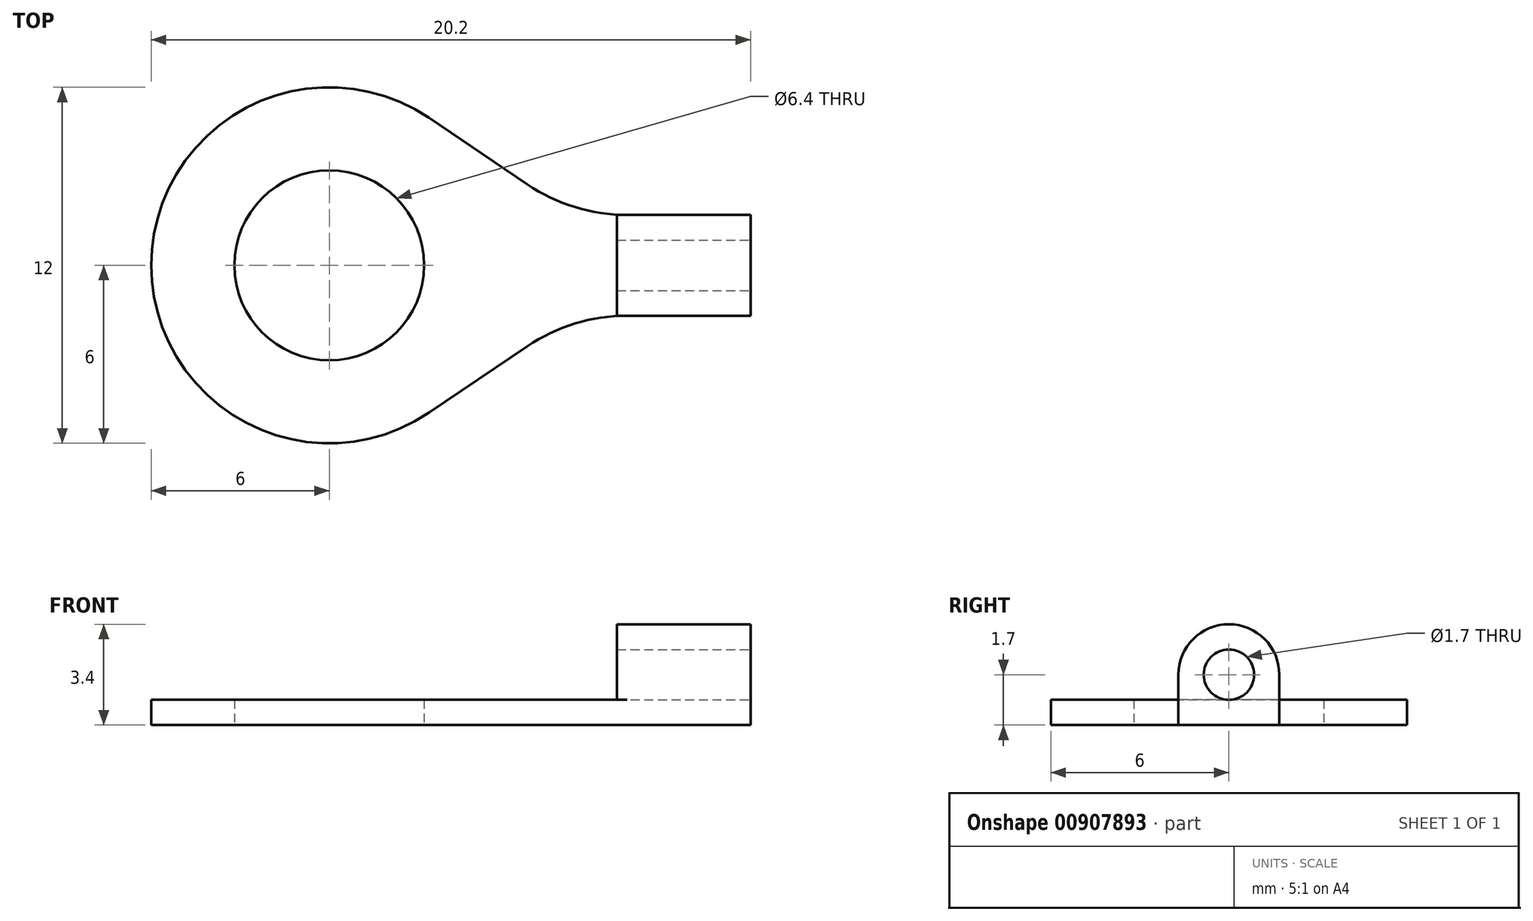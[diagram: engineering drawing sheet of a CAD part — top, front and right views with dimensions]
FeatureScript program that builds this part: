
annotation { "Feature Type Name" : "Feature", "Feature Type Description" : "" }
export const myFeature = defineFeature(function(context is Context, id is Id, definition is map)
    precondition{}
    {
        {
            var Q0;
            Q0=qCreatedBy(makeId("Top.planeOp"),FACE);
            var sketch = newSketch(context, id + "F0", { "sketchPlane" : qUnion([Q0])});
            skLineSegment(sketch, "E0.left", {"start": v(0, 6) * mm, "end": v(0, 6) * mm});
            skLineSegment(sketch, "E0.right", {"start": v(20.2, 4.3) * mm, "end": v(20.2, 7.7) * mm});
            skPoint(sketch, "E1.visualSharp", {"position": v(0, 12) * mm});
            skArc(sketch, "E1.filletArc", {"start": v(6, 12) * mm, "mid": v(1.76, 10.24) * mm, "end": v(0, 6) * mm});
            skPoint(sketch, "E2.visualSharp", {"position": v(0, 0) * mm});
            skArc(sketch, "E2.filletArc", {"start": v(0, 6) * mm, "mid": v(1.76, 1.76) * mm, "end": v(6, 0) * mm});
            skLineSegment(sketch, "E3.bottom", {"start": v(20.2, 4.3) * mm, "end": v(16.04, 4.3) * mm});
            skLineSegment(sketch, "E3.top", {"start": v(20.2, 7.7) * mm, "end": v(16.04, 7.7) * mm});
            skPoint(sketch, "E3.middle", {"position": v(20.2, 6) * mm});
            skArc(sketch, "E4", {"start": v(9.36, 10.97) * mm, "mid": v(0, 6) * mm, "end": v(9.36, 1.03) * mm});
            skCircle(sketch, "E5", {"center": v(6, 6) * mm, "radius": 3.2 * mm});
            skLineSegment(sketch, "E6", {"start": v(12.68, 8.73) * mm, "end": v(9.36, 10.97) * mm});
            skLineSegment(sketch, "E7", {"start": v(12.68, 3.27) * mm, "end": v(9.36, 1.03) * mm});
            skPoint(sketch, "E8.visualSharp", {"position": v(14.2, 7.7) * mm});
            skArc(sketch, "E8.filletArc", {"start": v(12.68, 8.73) * mm, "mid": v(14.28, 7.96) * mm, "end": v(16.04, 7.7) * mm});
            skPoint(sketch, "E9.visualSharp", {"position": v(14.2, 4.3) * mm});
            skArc(sketch, "E9.filletArc", {"start": v(16.04, 4.3) * mm, "mid": v(14.28, 4.04) * mm, "end": v(12.68, 3.27) * mm});
            skPoint(sketch, "E3.right.end.orphan", {"position": v(15.7, 7.7) * mm});
            skPoint(sketch, "E3.right.start.orphan", {"position": v(15.7, 4.3) * mm});
            skPoint(sketch, "E10.orphan", {"position": v(24.7, 7.7) * mm});
            skPoint(sketch, "E11.orphan", {"position": v(24.7, 4.3) * mm});
            skPoint(sketch, "E0.top.end.orphan", {"position": v(20.2, 12) * mm});
            skPoint(sketch, "E0.bottom.end.orphan", {"position": v(20.2, 0) * mm});
            skSolve(sketch);
        }
        {
            var Q0;
            Q0=makeQuery(id+"F0.imprint","IMPRINT",FACE,{"disambiguationData":[TD([[makeQuery(id+"F0.imprint","IMPRINT",EDGE,{"derivedFrom":sQuery(id+"F0.wireOp",EDGE,"E0.right")}),1.0]])]});
            extrude(context, id + "F1", {"entities" : qUnion([Q0]), "depth" : 0.85 * mm, "offsetDistance" : 25 * mm});
        }
        {
            var Q0;
            Q0=makeQuery(id+"F1.opExtrude","CAP_FACE",FACE,{"disambiguationData":[OSD([sQuery(id+"F0.wireOp",EDGE,"E0.right"),sQuery(id+"F0.wireOp",EDGE,"E3.bottom"),sQuery(id+"F0.wireOp",EDGE,"E3.top"),sQuery(id+"F0.wireOp",EDGE,"E4"),sQuery(id+"F0.wireOp",EDGE,"E5"),sQuery(id+"F0.wireOp",EDGE,"E6"),sQuery(id+"F0.wireOp",EDGE,"E7"),sQuery(id+"F0.wireOp",EDGE,"E8.filletArc"),sQuery(id+"F0.wireOp",EDGE,"E9.filletArc")])],"isStart":false});
            var sketch = newSketch(context, id + "F2", { "sketchPlane" : qUnion([Q0])});
            skLineSegment(sketch, "E12.bottom", {"start": v(20.2, 7.7) * mm, "end": v(15.7, 7.7) * mm});
            skLineSegment(sketch, "E12.top", {"start": v(20.2, 4.3) * mm, "end": v(15.7, 4.3) * mm});
            skLineSegment(sketch, "E12.left", {"start": v(20.2, 7.7) * mm, "end": v(20.2, 4.3) * mm});
            skLineSegment(sketch, "E12.right", {"start": v(15.7, 7.7) * mm, "end": v(15.7, 4.3) * mm});
            skSolve(sketch);
        }
        {
            var Q0;
            {var subQ0=sQuery(id+"F2.wireOp",EDGE,"E12.left");Q0=makeQuery(id+"F2.imprint","IMPRINT",FACE,{"disambiguationData":[TD([[makeQuery(id+"F2.imprint","IMPRINT",EDGE,{"derivedFrom":subQ0}),1.0]])]});}
            extrude(context, id + "F3", {"entities" : qUnion([Q0]), "operationType" : NewBodyOperationType.ADD, "depth" : 2.55 * mm, "offsetDistance" : 25 * mm});
        }
        {
            var Q0;
            Q0=makeQuery(id+"F3.opExtrude","CAP_EDGE",EDGE,{"disambiguationData":[OSD([sQuery(id+"F2.wireOp",EDGE,"E12.bottom")])],"isStart":false});
            var Q1;
            Q1=makeQuery(id+"F3.opExtrude","CAP_EDGE",EDGE,{"disambiguationData":[OSD([sQuery(id+"F2.wireOp",EDGE,"E12.top")])],"isStart":false});
            fillet(context, id + "F4", {"entities" : qUnion([Q0, Q1]), "radius" : 1.7 * mm, "tangentPropagation" : true, "allowEdgeOverflow" : false});
        }
        {
            var Q0;
            Q0=makeQuery(id+"F3.boolean.opBoolean","MERGE",FACE,{"derivedFrom":[makeQuery(id+"F1.opExtrude","SWEPT_FACE",FACE,{"disambiguationData":[OSD([sQuery(id+"F0.wireOp",EDGE,"E0.right")])]}),makeQuery(id+"F3.opExtrude","SWEPT_FACE",FACE,{"disambiguationData":[OSD([sQuery(id+"F2.wireOp",EDGE,"E12.left")])]})]});
            var sketch = newSketch(context, id + "F5", { "sketchPlane" : qUnion([Q0])});
            skCircle(sketch, "E13", {"center": v(6, 1.7) * mm, "radius": 0.85 * mm});
            skSolve(sketch);
        }
        {
            var Q0;
            Q0=makeQuery(id+"F5.imprint","IMPRINT",FACE,{"disambiguationData":[TD([[makeQuery(id+"F5.imprint","IMPRINT",EDGE,{"derivedFrom":sQuery(id+"F5.wireOp",EDGE,"E13")}),1.0]])]});
            extrude(context, id + "F6", {"entities" : qUnion([Q0]), "operationType" : NewBodyOperationType.REMOVE, "oppositeDirection" : true, "depth" : 25 * mm, "offsetDistance" : 25 * mm});
        }
    });
